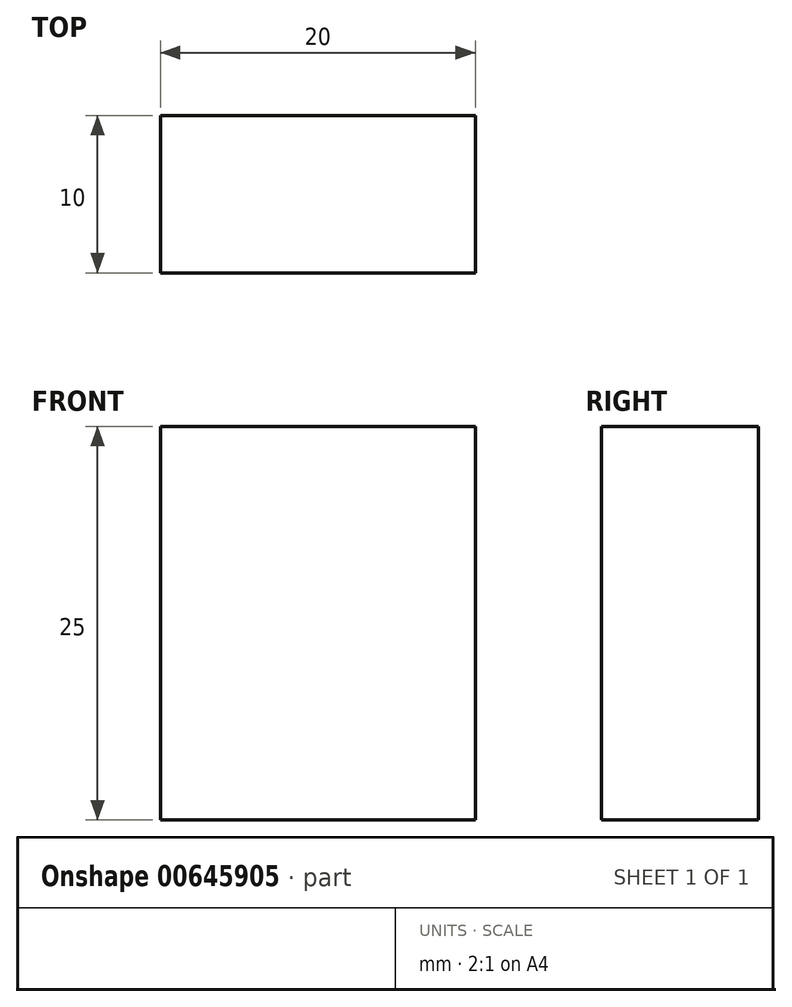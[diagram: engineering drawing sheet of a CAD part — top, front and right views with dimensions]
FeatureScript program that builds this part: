
annotation { "Feature Type Name" : "Feature", "Feature Type Description" : "" }
export const myFeature = defineFeature(function(context is Context, id is Id, definition is map)
    precondition{}
    {
        {
            var Q0;
            Q0=qCreatedBy(makeId("Top.planeOp"),FACE);
            var sketch = newSketch(context, id + "F0", { "sketchPlane" : qUnion([Q0])});
            skLineSegment(sketch, "E0", {"start": v(0.99, -1.98) * mm, "end": v(20.99, -1.98) * mm});
            skLineSegment(sketch, "E1", {"start": v(20.99, -1.98) * mm, "end": v(20.99, -11.98) * mm});
            skLineSegment(sketch, "E2", {"start": v(20.99, -11.98) * mm, "end": v(0.99, -11.98) * mm});
            skLineSegment(sketch, "E3", {"start": v(0.99, -11.98) * mm, "end": v(0.99, -1.98) * mm});
            skSolve(sketch);
        }
        {
            var Q0;
            Q0=makeQuery(id+"F0.imprint","IMPRINT",FACE,{"disambiguationData":[TD([[makeQuery(id+"F0.imprint","IMPRINT",EDGE,{"derivedFrom":sQuery(id+"F0.wireOp",EDGE,"E0")}),-1.0]])]});
            extrude(context, id + "F1", {"entities" : qUnion([Q0]), "depth" : 25 * mm, "offsetDistance" : 25 * mm});
        }
    });
